# Revit family: Non-Composite Decking-Side
name_source: partatom
category: Detail Items
revit_build: Autodesk Revit Architecture 2012 (Build: 20110210_1515)
units: mm (PartAtom-declared; Revit-internal decimal feet)

## types (21) — shared parameters

## per-type parameters (varying)
| type | Gauge | Height | Keynote | Rib Max | Rib Min | Width |
| 1.5 NC 18 | 18 | 0' - 1 1/2" | 05 31 00.B10 | 0' - 2 7/16" | 0' - 1 3/4" | 0' - 6" |
| 3.0 NC 16 | 16 | 0' - 3" | 05 31 00.B18 | 0' - 7 3/16" | 0' - 4 3/4" | 1' - 0" |
| 2.0 NC 16 | 16 | 0' - 2" | 05 31 00.B14 | 0' - 6 15/16" | 0' - 5" | 1' - 0" |
| .6 NC 22 | 22 | 0' - 0 9/16" | 05 31 00.B1 | 0' - 1 3/4" | 0' - 0 3/4" | 0' - 2 1/2" |
| 1.0 NC 18 | 18 | 0' - 1" | 05 31 00.B5 | 0' - 2 13/16" | 0' - 1 1/8" | 0' - 4" |
| .6 NC 24 | 24 | 0' - 0 9/16" | 05 31 00.B2 | 0' - 1 3/4" | 0' - 0 3/4" | 0' - 2 1/2" |
| .6 NC 28 | 28 | 0' - 0 9/16" | 05 31 00.B4 | 0' - 1 3/4" | 0' - 0 3/4" | 0' - 2 1/2" |
| .6 NC 26 | 26 | 0' - 0 9/16" | 05 31 00.B3 | 0' - 1 3/4" | 0' - 0 3/4" | 0' - 2 1/2" |
| 1.0 NC 20 | 20 | 0' - 1" | 05 31 00.B6 | 0' - 2 13/16" | 0' - 1 1/8" | 0' - 4" |
| 1.0 NC 22 | 22 | 0' - 1" | 05 31 00.B7 | 0' - 2 13/16" | 0' - 1 1/8" | 0' - 4" |
| 1.0 NC 24 | 24 | 0' - 1" | 05 31 00.B8 | 0' - 2 13/16" | 0' - 1 1/8" | 0' - 4" |
| 1.0 NC 26 | 26 | 0' - 1" | 05 31 00.B9 | 0' - 2 13/16" | 0' - 1 1/8" | 0' - 4" |
| 1.5 NC 20 | 20 | 0' - 1 1/2" | 05 31 00.B11 | 0' - 2 7/16" | 0' - 1 3/4" | 0' - 6" |
| 1.5 NC 22 | 22 | 0' - 1 1/2" | 05 31 00.B12 | 0' - 2 7/16" | 0' - 1 3/4" | 0' - 6" |
| 1.5 NC 24 | 24 | 0' - 1 1/2" | 05 31 00.B13 | 0' - 2 7/16" | 0' - 1 3/4" | 0' - 6" |
| 2.0 NC 18 | 18 | 0' - 2" | 05 31 00.B15 | 0' - 6 15/16" | 0' - 5" | 1' - 0" |
| 2.0 NC 20 | 20 | 0' - 2" | 05 31 00.B16 | 0' - 6 15/16" | 0' - 5" | 1' - 0" |
| 2.0 NC 22 | 22 | 0' - 2" | 05 31 00.B17 | 0' - 6 15/16" | 0' - 5" | 1' - 0" |
| 3.0 NC 18 | 18 | 0' - 3" | 05 31 00.B19 | 0' - 7 3/16" | 0' - 4 3/4" | 1' - 0" |
| 3.0 NC 20 | 20 | 0' - 3" | 05 31 00.B20 | 0' - 7 3/16" | 0' - 4 3/4" | 1' - 0" |
| 3.0 NC 22 | 22 | 0' - 3" | 05 31 00.B21 | 0' - 7 3/16" | 0' - 4 3/4" | 1' - 0" |

## geometry (parser evidence)
native form markers: Sweep x1
no freeform markers — native parametric forms only
